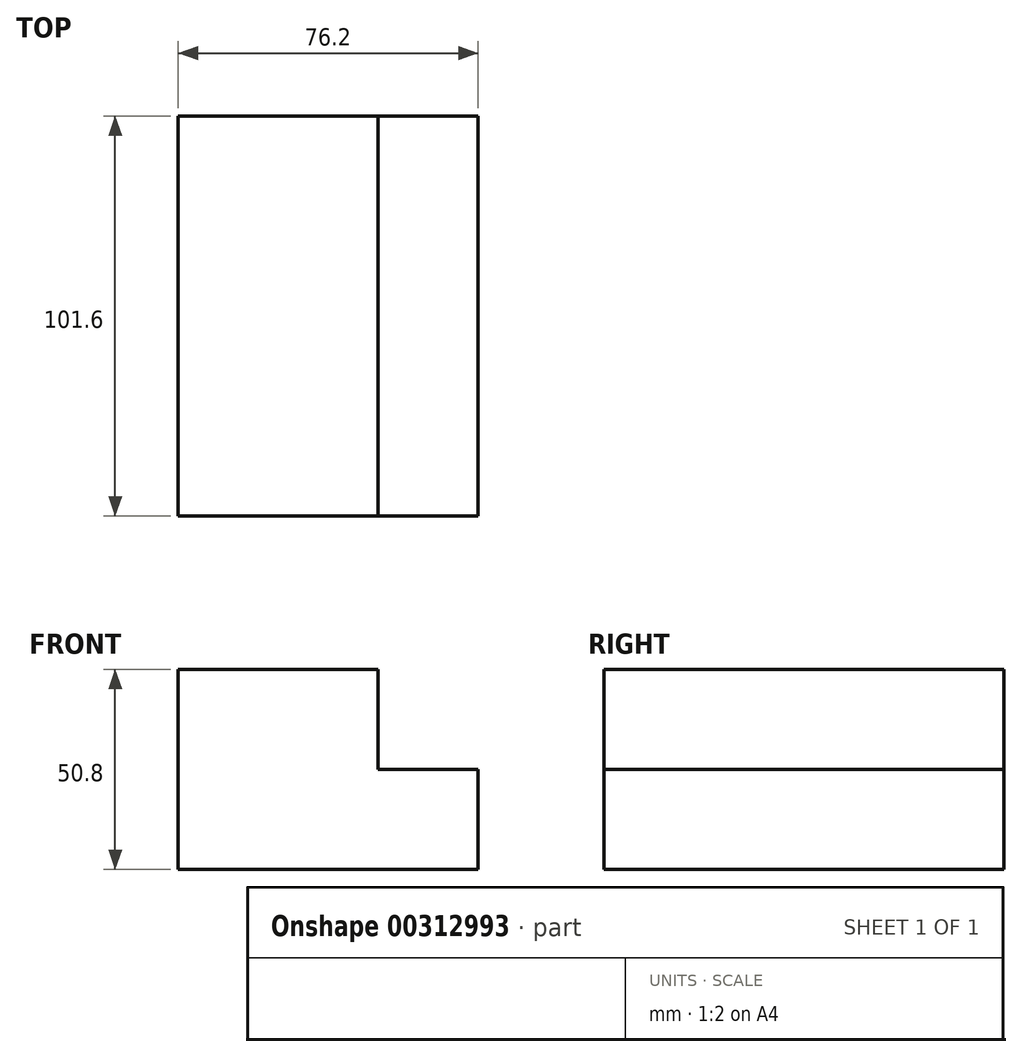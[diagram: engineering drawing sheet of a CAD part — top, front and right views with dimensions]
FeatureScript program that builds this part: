
annotation { "Feature Type Name" : "Feature", "Feature Type Description" : "" }
export const myFeature = defineFeature(function(context is Context, id is Id, definition is map)
    precondition{}
    {
        {
            var Q0;
            Q0=qCreatedBy(makeId("Front.planeOp"),FACE);
            var sketch = newSketch(context, id + "F0", { "sketchPlane" : qUnion([Q0])});
            skLineSegment(sketch, "E0", {"start": v(-45.39, -45.2) * mm, "end": v(30.81, -45.2) * mm});
            skLineSegment(sketch, "E1", {"start": v(30.81, -45.2) * mm, "end": v(30.81, -19.8) * mm});
            skLineSegment(sketch, "E2", {"start": v(30.81, -19.8) * mm, "end": v(5.41, -19.8) * mm});
            skLineSegment(sketch, "E3", {"start": v(5.41, -19.8) * mm, "end": v(5.41, 5.6) * mm});
            skLineSegment(sketch, "E4", {"start": v(5.41, 5.6) * mm, "end": v(-45.39, 5.6) * mm});
            skLineSegment(sketch, "E5", {"start": v(-45.39, 5.6) * mm, "end": v(-45.39, -45.2) * mm});
            skSolve(sketch);
        }
        {
            var Q0;
            Q0=makeQuery(id+"F0.imprint","IMPRINT",FACE,{"disambiguationData":[TD([[makeQuery(id+"F0.imprint","IMPRINT",EDGE,{"derivedFrom":sQuery(id+"F0.wireOp",EDGE,"E0")}),1.0]])]});
            extrude(context, id + "F1", {"entities" : qUnion([Q0]), "depth" : 101.6 * mm});
        }
    });
